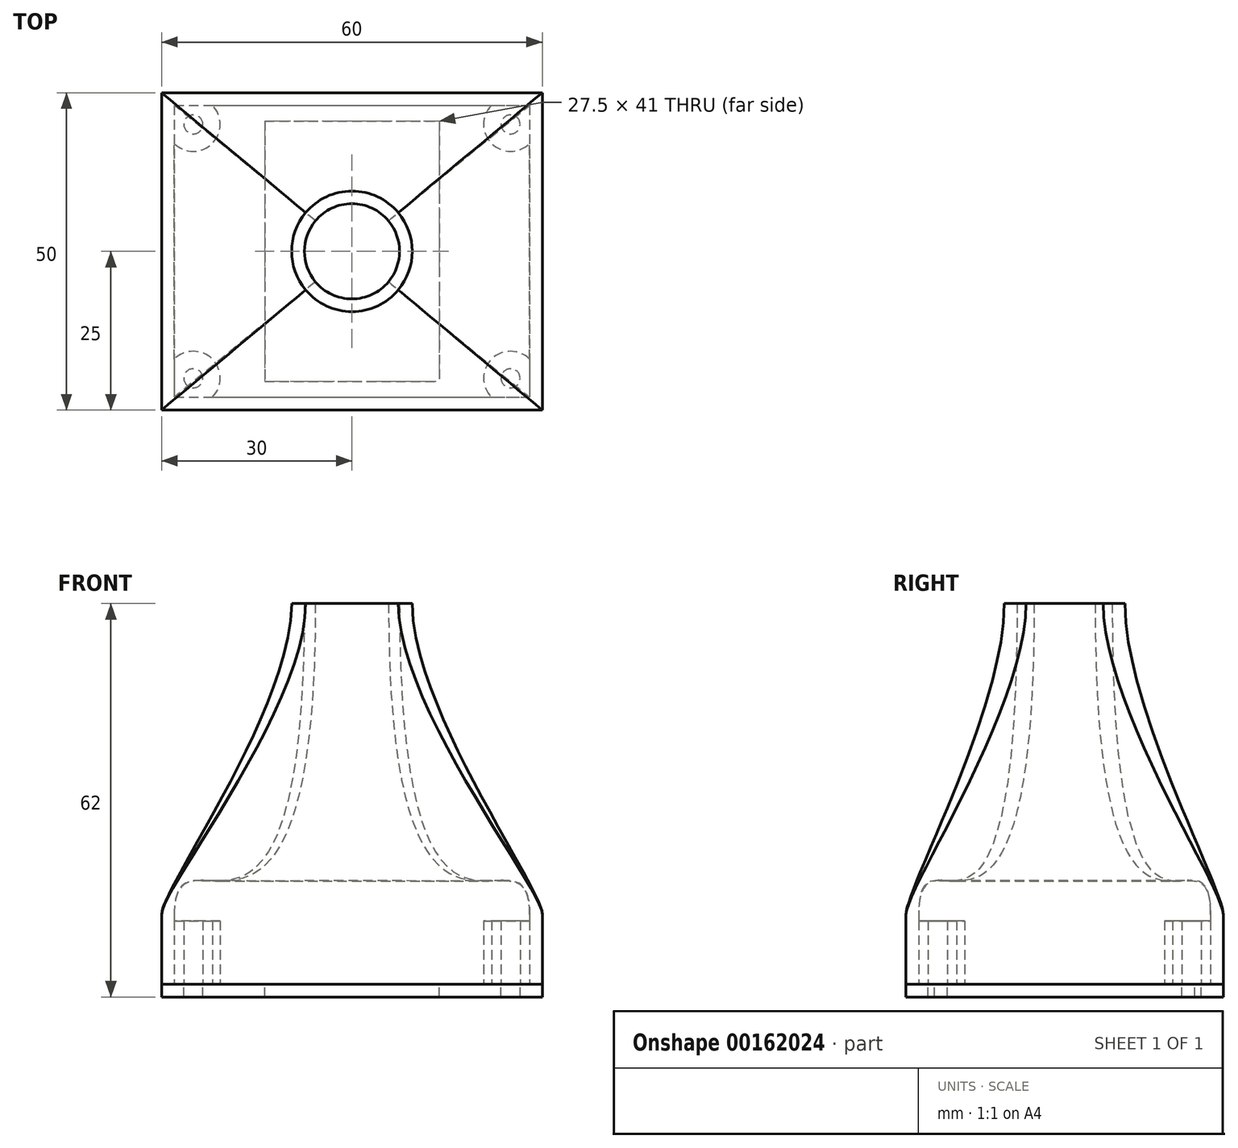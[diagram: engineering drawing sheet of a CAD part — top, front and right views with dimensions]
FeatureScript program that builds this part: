
annotation { "Feature Type Name" : "Feature", "Feature Type Description" : "" }
export const myFeature = defineFeature(function(context is Context, id is Id, definition is map)
    precondition{}
    {
        {
            var Q0;
            Q0=qCreatedBy(makeId("Top.planeOp"),FACE);
            var sketch = newSketch(context, id + "F0", { "sketchPlane" : qUnion([Q0])});
            skLineSegment(sketch, "E0.bottom", {"start": v(0, 0) * mm, "end": v(60, 0) * mm});
            skLineSegment(sketch, "E0.top", {"start": v(0, 50) * mm, "end": v(60, 50) * mm});
            skLineSegment(sketch, "E0.left", {"start": v(0, 0) * mm, "end": v(0, 50) * mm});
            skLineSegment(sketch, "E0.right", {"start": v(60, 0) * mm, "end": v(60, 50) * mm});
            skCircle(sketch, "E1", {"center": v(5, 45) * mm, "radius": 1.5 * mm});
            skCircle(sketch, "E2", {"center": v(55, 45) * mm, "radius": 1.5 * mm});
            skCircle(sketch, "E3", {"center": v(55, 5) * mm, "radius": 1.5 * mm});
            skCircle(sketch, "E4", {"center": v(5, 5) * mm, "radius": 1.5 * mm});
            skLineSegment(sketch, "E5.bottom", {"start": v(16.25, 45.5) * mm, "end": v(43.75, 45.5) * mm});
            skLineSegment(sketch, "E5.top", {"start": v(16.25, 4.5) * mm, "end": v(43.75, 4.5) * mm});
            skLineSegment(sketch, "E5.left", {"start": v(16.25, 45.5) * mm, "end": v(16.25, 4.5) * mm});
            skLineSegment(sketch, "E5.right", {"start": v(43.75, 45.5) * mm, "end": v(43.75, 4.5) * mm});
            skLineSegment(sketch, "E6", {"start": v(30, 50) * mm, "end": v(30, 0) * mm, "construction": true});
            skPoint(sketch, "E6.endSnap0", {"position": v(30, 45.5) * mm});
            skLineSegment(sketch, "E7", {"start": v(0, 25) * mm, "end": v(60, 25) * mm, "construction": true});
            skLineSegment(sketch, "E8", {"start": v(16.25, 45.5) * mm, "end": v(0, 50) * mm, "construction": true});
            skLineSegment(sketch, "E9", {"start": v(16.25, 4.5) * mm, "end": v(0, 0) * mm, "construction": true});
            skLineSegment(sketch, "E10", {"start": v(5, 45) * mm, "end": v(0, 45) * mm, "construction": true});
            skLineSegment(sketch, "E11", {"start": v(5, 5) * mm, "end": v(0, 5) * mm, "construction": true});
            skLineSegment(sketch, "E12", {"start": v(55, 5) * mm, "end": v(60, 5) * mm, "construction": true});
            skLineSegment(sketch, "E13", {"start": v(55, 45) * mm, "end": v(60, 45) * mm, "construction": true});
            skLineSegment(sketch, "E14", {"start": v(5, 45) * mm, "end": v(5, 50) * mm, "construction": true});
            skLineSegment(sketch, "E15", {"start": v(55, 45) * mm, "end": v(55, 50) * mm, "construction": true});
            skLineSegment(sketch, "E16", {"start": v(55, 5) * mm, "end": v(55, 0) * mm, "construction": true});
            skLineSegment(sketch, "E17", {"start": v(5, 5) * mm, "end": v(5, 0) * mm, "construction": true});
            skLineSegment(sketch, "E18.0", {"start": v(2, 48) * mm, "end": v(58, 48) * mm});
            skLineSegment(sketch, "E18.1", {"start": v(2, 2) * mm, "end": v(2, 48) * mm});
            skLineSegment(sketch, "E18.2", {"start": v(2, 2) * mm, "end": v(58, 2) * mm});
            skLineSegment(sketch, "E18.3", {"start": v(58, 2) * mm, "end": v(58, 48) * mm});
            skCircle(sketch, "E19", {"center": v(5, 5) * mm, "radius": 4.24 * mm});
            skCircle(sketch, "E20", {"center": v(55, 5) * mm, "radius": 4.24 * mm});
            skCircle(sketch, "E21", {"center": v(55, 45) * mm, "radius": 4.24 * mm});
            skCircle(sketch, "E22", {"center": v(5, 45) * mm, "radius": 4.24 * mm});
            skSolve(sketch);
        }
        {
            var Q0;
            Q0=makeQuery(id+"F0.imprint","IMPRINT",FACE,{"disambiguationData":[TD([[makeQuery(id+"F0.imprint","IMPRINT",EDGE,{"derivedFrom":sQuery(id+"F0.wireOp",EDGE,"E5.bottom")}),1.0]])]});
            var Q1;
            Q1=makeQuery(id+"F0.imprint","IMPRINT",FACE,{"disambiguationData":[TD([[makeQuery(id+"F0.imprint","IMPRINT",EDGE,{"derivedFrom":sQuery(id+"F0.wireOp",EDGE,"E1")}),-1.0]])]});
            var Q2;
            Q2=makeQuery(id+"F0.imprint","IMPRINT",FACE,{"disambiguationData":[TD([[makeQuery(id+"F0.imprint","IMPRINT",EDGE,{"derivedFrom":sQuery(id+"F0.wireOp",EDGE,"E0.bottom")}),1.0]])]});
            var Q3;
            {var subQ0=sQuery(id+"F0.wireOp",EDGE,"E22");var subQ1=sQuery(id+"F0.wireOp",EDGE,"E18.1");var subQ3=makeQuery(id+"F0.imprint","INTERSECT",VERTEX,{"derivedFrom":[subQ1,subQ0]});Q3=makeQuery(id+"F0.imprint","IMPRINT",FACE,{"disambiguationData":[TD([[makeQuery(id+"F0.imprint","IMPRINT",EDGE,{"disambiguationData":[TD([[subQ3,-1.0]])],"derivedFrom":subQ1}),1.0]])]});}
            var Q4;
            {var subQ0=sQuery(id+"F0.wireOp",EDGE,"E22");var subQ1=sQuery(id+"F0.wireOp",EDGE,"E18.0");var subQ3=makeQuery(id+"F0.imprint","INTERSECT",VERTEX,{"derivedFrom":[subQ1,subQ0]});Q4=makeQuery(id+"F0.imprint","IMPRINT",FACE,{"disambiguationData":[TD([[makeQuery(id+"F0.imprint","IMPRINT",EDGE,{"disambiguationData":[TD([[subQ3,1.0]])],"derivedFrom":subQ1}),1.0]])]});}
            var Q5;
            {var subQ0=sQuery(id+"F0.wireOp",EDGE,"E21");var subQ1=sQuery(id+"F0.wireOp",EDGE,"E18.3");var subQ3=makeQuery(id+"F0.imprint","INTERSECT",VERTEX,{"derivedFrom":[subQ1,subQ0]});Q5=makeQuery(id+"F0.imprint","IMPRINT",FACE,{"disambiguationData":[TD([[makeQuery(id+"F0.imprint","IMPRINT",EDGE,{"disambiguationData":[TD([[subQ3,-1.0]])],"derivedFrom":subQ1}),-1.0]])]});}
            var Q6;
            Q6=makeQuery(id+"F0.imprint","IMPRINT",FACE,{"disambiguationData":[TD([[makeQuery(id+"F0.imprint","IMPRINT",EDGE,{"derivedFrom":sQuery(id+"F0.wireOp",EDGE,"E2")}),-1.0]])]});
            var Q7;
            {var subQ0=sQuery(id+"F0.wireOp",EDGE,"E21");var subQ1=sQuery(id+"F0.wireOp",EDGE,"E18.0");var subQ3=makeQuery(id+"F0.imprint","INTERSECT",VERTEX,{"derivedFrom":[subQ1,subQ0]});Q7=makeQuery(id+"F0.imprint","IMPRINT",FACE,{"disambiguationData":[TD([[makeQuery(id+"F0.imprint","IMPRINT",EDGE,{"disambiguationData":[TD([[subQ3,-1.0]])],"derivedFrom":subQ1}),1.0]])]});}
            var Q8;
            {var subQ0=sQuery(id+"F0.wireOp",EDGE,"E20");var subQ1=sQuery(id+"F0.wireOp",EDGE,"E18.3");var subQ3=makeQuery(id+"F0.imprint","INTERSECT",VERTEX,{"derivedFrom":[subQ1,subQ0]});Q8=makeQuery(id+"F0.imprint","IMPRINT",FACE,{"disambiguationData":[TD([[makeQuery(id+"F0.imprint","IMPRINT",EDGE,{"disambiguationData":[TD([[subQ3,1.0]])],"derivedFrom":subQ1}),-1.0]])]});}
            var Q9;
            Q9=makeQuery(id+"F0.imprint","IMPRINT",FACE,{"disambiguationData":[TD([[makeQuery(id+"F0.imprint","IMPRINT",EDGE,{"derivedFrom":sQuery(id+"F0.wireOp",EDGE,"E3")}),-1.0]])]});
            var Q10;
            {var subQ0=sQuery(id+"F0.wireOp",EDGE,"E20");var subQ1=sQuery(id+"F0.wireOp",EDGE,"E18.2");var subQ3=makeQuery(id+"F0.imprint","INTERSECT",VERTEX,{"derivedFrom":[subQ1,subQ0]});Q10=makeQuery(id+"F0.imprint","IMPRINT",FACE,{"disambiguationData":[TD([[makeQuery(id+"F0.imprint","IMPRINT",EDGE,{"disambiguationData":[TD([[subQ3,-1.0]])],"derivedFrom":subQ1}),-1.0]])]});}
            var Q11;
            Q11=makeQuery(id+"F0.imprint","IMPRINT",FACE,{"disambiguationData":[TD([[makeQuery(id+"F0.imprint","IMPRINT",EDGE,{"derivedFrom":sQuery(id+"F0.wireOp",EDGE,"E4")}),-1.0]])]});
            var Q12;
            {var subQ0=sQuery(id+"F0.wireOp",EDGE,"E19");var subQ1=sQuery(id+"F0.wireOp",EDGE,"E18.1");var subQ3=makeQuery(id+"F0.imprint","INTERSECT",VERTEX,{"derivedFrom":[subQ1,subQ0]});Q12=makeQuery(id+"F0.imprint","IMPRINT",FACE,{"disambiguationData":[TD([[makeQuery(id+"F0.imprint","IMPRINT",EDGE,{"disambiguationData":[TD([[subQ3,1.0]])],"derivedFrom":subQ1}),1.0]])]});}
            var Q13;
            {var subQ0=sQuery(id+"F0.wireOp",EDGE,"E19");var subQ1=sQuery(id+"F0.wireOp",EDGE,"E18.2");var subQ3=makeQuery(id+"F0.imprint","INTERSECT",VERTEX,{"derivedFrom":[subQ1,subQ0]});Q13=makeQuery(id+"F0.imprint","IMPRINT",FACE,{"disambiguationData":[TD([[makeQuery(id+"F0.imprint","IMPRINT",EDGE,{"disambiguationData":[TD([[subQ3,1.0]])],"derivedFrom":subQ1}),-1.0]])]});}
            extrude(context, id + "F1", {"entities" : qUnion([Q0, Q1, Q2, Q3, Q4, Q5, Q6, Q7, Q8, Q9, Q10, Q11, Q12, Q13]), "oppositeDirection" : true, "depth" : 2 * mm});
        }
        {
            var Q0;
            Q0=makeQuery(id+"F0.imprint","IMPRINT",FACE,{"disambiguationData":[TD([[makeQuery(id+"F0.imprint","IMPRINT",EDGE,{"derivedFrom":sQuery(id+"F0.wireOp",EDGE,"E0.bottom")}),1.0]])]});
            var Q1;
            {var subQ0=sQuery(id+"F0.wireOp",EDGE,"E21");var subQ1=sQuery(id+"F0.wireOp",EDGE,"E18.3");var subQ3=makeQuery(id+"F0.imprint","INTERSECT",VERTEX,{"derivedFrom":[subQ1,subQ0]});Q1=makeQuery(id+"F0.imprint","IMPRINT",FACE,{"disambiguationData":[TD([[makeQuery(id+"F0.imprint","IMPRINT",EDGE,{"disambiguationData":[TD([[subQ3,-1.0]])],"derivedFrom":subQ1}),-1.0]])]});}
            var Q2;
            Q2=makeQuery(id+"F0.imprint","IMPRINT",FACE,{"disambiguationData":[TD([[makeQuery(id+"F0.imprint","IMPRINT",EDGE,{"derivedFrom":sQuery(id+"F0.wireOp",EDGE,"E2")}),-1.0]])]});
            var Q3;
            {var subQ0=sQuery(id+"F0.wireOp",EDGE,"E21");var subQ1=sQuery(id+"F0.wireOp",EDGE,"E18.0");var subQ3=makeQuery(id+"F0.imprint","INTERSECT",VERTEX,{"derivedFrom":[subQ1,subQ0]});Q3=makeQuery(id+"F0.imprint","IMPRINT",FACE,{"disambiguationData":[TD([[makeQuery(id+"F0.imprint","IMPRINT",EDGE,{"disambiguationData":[TD([[subQ3,-1.0]])],"derivedFrom":subQ1}),1.0]])]});}
            var Q4;
            {var subQ0=sQuery(id+"F0.wireOp",EDGE,"E20");var subQ1=sQuery(id+"F0.wireOp",EDGE,"E18.2");var subQ3=makeQuery(id+"F0.imprint","INTERSECT",VERTEX,{"derivedFrom":[subQ1,subQ0]});Q4=makeQuery(id+"F0.imprint","IMPRINT",FACE,{"disambiguationData":[TD([[makeQuery(id+"F0.imprint","IMPRINT",EDGE,{"disambiguationData":[TD([[subQ3,-1.0]])],"derivedFrom":subQ1}),-1.0]])]});}
            var Q5;
            {var subQ0=sQuery(id+"F0.wireOp",EDGE,"E20");var subQ1=sQuery(id+"F0.wireOp",EDGE,"E18.3");var subQ3=makeQuery(id+"F0.imprint","INTERSECT",VERTEX,{"derivedFrom":[subQ1,subQ0]});Q5=makeQuery(id+"F0.imprint","IMPRINT",FACE,{"disambiguationData":[TD([[makeQuery(id+"F0.imprint","IMPRINT",EDGE,{"disambiguationData":[TD([[subQ3,1.0]])],"derivedFrom":subQ1}),-1.0]])]});}
            var Q6;
            Q6=makeQuery(id+"F0.imprint","IMPRINT",FACE,{"disambiguationData":[TD([[makeQuery(id+"F0.imprint","IMPRINT",EDGE,{"derivedFrom":sQuery(id+"F0.wireOp",EDGE,"E3")}),-1.0]])]});
            var Q7;
            {var subQ0=sQuery(id+"F0.wireOp",EDGE,"E19");var subQ1=sQuery(id+"F0.wireOp",EDGE,"E18.1");var subQ3=makeQuery(id+"F0.imprint","INTERSECT",VERTEX,{"derivedFrom":[subQ1,subQ0]});Q7=makeQuery(id+"F0.imprint","IMPRINT",FACE,{"disambiguationData":[TD([[makeQuery(id+"F0.imprint","IMPRINT",EDGE,{"disambiguationData":[TD([[subQ3,1.0]])],"derivedFrom":subQ1}),1.0]])]});}
            var Q8;
            Q8=makeQuery(id+"F0.imprint","IMPRINT",FACE,{"disambiguationData":[TD([[makeQuery(id+"F0.imprint","IMPRINT",EDGE,{"derivedFrom":sQuery(id+"F0.wireOp",EDGE,"E4")}),-1.0]])]});
            var Q9;
            {var subQ0=sQuery(id+"F0.wireOp",EDGE,"E19");var subQ1=sQuery(id+"F0.wireOp",EDGE,"E18.2");var subQ3=makeQuery(id+"F0.imprint","INTERSECT",VERTEX,{"derivedFrom":[subQ1,subQ0]});Q9=makeQuery(id+"F0.imprint","IMPRINT",FACE,{"disambiguationData":[TD([[makeQuery(id+"F0.imprint","IMPRINT",EDGE,{"disambiguationData":[TD([[subQ3,1.0]])],"derivedFrom":subQ1}),-1.0]])]});}
            var Q10;
            {var subQ0=sQuery(id+"F0.wireOp",EDGE,"E22");var subQ1=sQuery(id+"F0.wireOp",EDGE,"E18.0");var subQ3=makeQuery(id+"F0.imprint","INTERSECT",VERTEX,{"derivedFrom":[subQ1,subQ0]});Q10=makeQuery(id+"F0.imprint","IMPRINT",FACE,{"disambiguationData":[TD([[makeQuery(id+"F0.imprint","IMPRINT",EDGE,{"disambiguationData":[TD([[subQ3,1.0]])],"derivedFrom":subQ1}),1.0]])]});}
            var Q11;
            Q11=makeQuery(id+"F0.imprint","IMPRINT",FACE,{"disambiguationData":[TD([[makeQuery(id+"F0.imprint","IMPRINT",EDGE,{"derivedFrom":sQuery(id+"F0.wireOp",EDGE,"E1")}),-1.0]])]});
            var Q12;
            {var subQ0=sQuery(id+"F0.wireOp",EDGE,"E22");var subQ1=sQuery(id+"F0.wireOp",EDGE,"E18.1");var subQ3=makeQuery(id+"F0.imprint","INTERSECT",VERTEX,{"derivedFrom":[subQ1,subQ0]});Q12=makeQuery(id+"F0.imprint","IMPRINT",FACE,{"disambiguationData":[TD([[makeQuery(id+"F0.imprint","IMPRINT",EDGE,{"disambiguationData":[TD([[subQ3,-1.0]])],"derivedFrom":subQ1}),1.0]])]});}
            extrude(context, id + "F2", {"entities" : qUnion([Q0, Q1, Q2, Q3, Q4, Q5, Q6, Q7, Q8, Q9, Q10, Q11, Q12]), "depth" : 10 * mm});
        }
        {
            var Q0;
            Q0=makeQuery(id+"F2.opExtrude","CAP_FACE",FACE,{"disambiguationData":[OSD([sQuery(id+"F0.wireOp",EDGE,"E0.bottom"),sQuery(id+"F0.wireOp",EDGE,"E0.top"),sQuery(id+"F0.wireOp",EDGE,"E0.left"),sQuery(id+"F0.wireOp",EDGE,"E0.right"),sQuery(id+"F0.wireOp",EDGE,"E1"),sQuery(id+"F0.wireOp",EDGE,"E2"),sQuery(id+"F0.wireOp",EDGE,"E3"),sQuery(id+"F0.wireOp",EDGE,"E4"),sQuery(id+"F0.wireOp",EDGE,"E18.0"),sQuery(id+"F0.wireOp",EDGE,"E18.1"),sQuery(id+"F0.wireOp",EDGE,"E18.2"),sQuery(id+"F0.wireOp",EDGE,"E18.3"),sQuery(id+"F0.wireOp",EDGE,"E19"),sQuery(id+"F0.wireOp",EDGE,"E20"),sQuery(id+"F0.wireOp",EDGE,"E21"),sQuery(id+"F0.wireOp",EDGE,"E22")])],"isStart":false});
            cPlane(context, id + "F3", {"entities" : qUnion([Q0]), "cplaneType" : CPlaneType.OFFSET, "offset" : 50 * mm, "width" : 150 * mm, "height" : 150 * mm});
        }
        {
            var Q0;
            Q0=qCreatedBy(id+"F3.planeOp",FACE);
            var sketch = newSketch(context, id + "F4", { "sketchPlane" : qUnion([Q0])});
            skLineSegment(sketch, "E23.bottom", {"start": v(0, 0) * mm, "end": v(60, 0) * mm, "construction": true});
            skLineSegment(sketch, "E23.top", {"start": v(0, 50) * mm, "end": v(60, 50) * mm});
            skLineSegment(sketch, "E23.left", {"start": v(0, 0) * mm, "end": v(0, 50) * mm, "construction": true});
            skLineSegment(sketch, "E23.right", {"start": v(60, 0) * mm, "end": v(60, 50) * mm, "construction": true});
            skLineSegment(sketch, "E24", {"start": v(0, 50) * mm, "end": v(60, 0) * mm, "construction": true});
            skCircle(sketch, "E25", {"center": v(30, 25) * mm, "radius": 7.5 * mm, "construction": true});
            skLineSegment(sketch, "E26", {"start": v(0, 0) * mm, "end": v(60, 50) * mm, "construction": true});
            skArc(sketch, "E27", {"start": v(22.7, 31.08) * mm, "mid": v(20.5, 25) * mm, "end": v(22.7, 18.92) * mm});
            skArc(sketch, "E28", {"start": v(37.3, 31.08) * mm, "mid": v(30, 34.5) * mm, "end": v(22.7, 31.08) * mm});
            skArc(sketch, "E29", {"start": v(37.3, 18.92) * mm, "mid": v(39.5, 25) * mm, "end": v(37.3, 31.08) * mm});
            skArc(sketch, "E30", {"start": v(22.7, 18.92) * mm, "mid": v(30, 15.5) * mm, "end": v(37.3, 18.92) * mm});
            skSolve(sketch);
        }
        {
            var Q0;
            Q0=makeQuery(id+"F2.opExtrude","CAP_FACE",FACE,{"disambiguationData":[OSD([sQuery(id+"F0.wireOp",EDGE,"E0.bottom"),sQuery(id+"F0.wireOp",EDGE,"E0.top"),sQuery(id+"F0.wireOp",EDGE,"E0.left"),sQuery(id+"F0.wireOp",EDGE,"E0.right"),sQuery(id+"F0.wireOp",EDGE,"E1"),sQuery(id+"F0.wireOp",EDGE,"E2"),sQuery(id+"F0.wireOp",EDGE,"E3"),sQuery(id+"F0.wireOp",EDGE,"E4"),sQuery(id+"F0.wireOp",EDGE,"E18.0"),sQuery(id+"F0.wireOp",EDGE,"E18.1"),sQuery(id+"F0.wireOp",EDGE,"E18.2"),sQuery(id+"F0.wireOp",EDGE,"E18.3"),sQuery(id+"F0.wireOp",EDGE,"E19"),sQuery(id+"F0.wireOp",EDGE,"E20"),sQuery(id+"F0.wireOp",EDGE,"E21"),sQuery(id+"F0.wireOp",EDGE,"E22")])],"isStart":false});
            var sketch = newSketch(context, id + "F5", { "sketchPlane" : qUnion([Q0])});
            skLineSegment(sketch, "E31.bottom", {"start": v(0, 50) * mm, "end": v(60, 50) * mm});
            skLineSegment(sketch, "E31.top", {"start": v(0, 0) * mm, "end": v(60, 0) * mm});
            skLineSegment(sketch, "E31.left", {"start": v(0, 50) * mm, "end": v(0, 0) * mm});
            skLineSegment(sketch, "E31.right", {"start": v(60, 50) * mm, "end": v(60, 0) * mm});
            skLineSegment(sketch, "E32.0", {"start": v(2, 48) * mm, "end": v(58, 48) * mm});
            skLineSegment(sketch, "E32.1", {"start": v(2, 48) * mm, "end": v(2, 2) * mm});
            skLineSegment(sketch, "E32.2", {"start": v(2, 2) * mm, "end": v(58, 2) * mm});
            skLineSegment(sketch, "E32.3", {"start": v(58, 48) * mm, "end": v(58, 2) * mm});
            skSolve(sketch);
        }
        {
            var Q0;
            Q0 = qSketchRegion(id + "F5", true);
            extrude(context, id + "F6", {"entities" : qUnion([Q0]), "operationType" : NewBodyOperationType.ADD, "depth" : 1 * mm});
        }
        {
            var Q0;
            Q0=makeQuery(id+"F6.opExtrude","CAP_FACE",FACE,{"disambiguationData":[OSD([sQuery(id+"F5.wireOp",EDGE,"E31.bottom"),sQuery(id+"F5.wireOp",EDGE,"E31.top"),sQuery(id+"F5.wireOp",EDGE,"E31.left"),sQuery(id+"F5.wireOp",EDGE,"E31.right"),sQuery(id+"F5.wireOp",EDGE,"E32.0"),sQuery(id+"F5.wireOp",EDGE,"E32.1"),sQuery(id+"F5.wireOp",EDGE,"E32.2"),sQuery(id+"F5.wireOp",EDGE,"E32.3")])],"isStart":false});
            var sketch = newSketch(context, id + "F7", { "sketchPlane" : qUnion([Q0])});
            skLineSegment(sketch, "E33.0", {"start": v(0, 0) * mm, "end": v(0, 50) * mm});
            skLineSegment(sketch, "E33.1", {"start": v(0, 0) * mm, "end": v(60, 0) * mm});
            skLineSegment(sketch, "E33.2", {"start": v(60, 0) * mm, "end": v(60, 50) * mm});
            skLineSegment(sketch, "E33.3", {"start": v(0, 50) * mm, "end": v(60, 50) * mm});
            skSolve(sketch);
        }
        {
            var Q1;
            Q1 = qSketchRegion(id + "F7", true);
            var Q2;
            Q2 = qSketchRegion(id + "F4", true);
            loft(context, id + "F8", {"operationType" : NewBodyOperationType.ADD, "startCondition" : LoftEndDerivativeType.NORMAL_TO_PROFILE, "startMagnitude" : .25, "endCondition" : LoftEndDerivativeType.NORMAL_TO_PROFILE, "endMagnitude" : 1, "sheetProfilesArray" : [{ "sheetProfileEntities" : qUnion([Q1]) }, { "sheetProfileEntities" : qUnion([Q2]) }]});
        }
        {
            var Q0;
            Q0=makeQuery(id+"F8.opLoft","CAP_FACE",FACE,{"disambiguationData":[OSD([makeQuery(id+"F4.imprint","IMPRINT",FACE,{"disambiguationData":[TD([[makeQuery(id+"F4.imprint","IMPRINT",EDGE,{"derivedFrom":sQuery(id+"F4.wireOp",EDGE,"E27")}),1.0]])]})])],"isStart":true});
            var sketch = newSketch(context, id + "F9", { "sketchPlane" : qUnion([Q0])});
            skArc(sketch, "E34", {"start": v(35.76, 29.8) * mm, "mid": v(30, 32.5) * mm, "end": v(24.24, 29.8) * mm});
            skArc(sketch, "E35", {"start": v(24.24, 20.2) * mm, "mid": v(30, 17.5) * mm, "end": v(35.76, 20.2) * mm});
            skArc(sketch, "E36", {"start": v(24.24, 29.8) * mm, "mid": v(22.5, 25) * mm, "end": v(24.24, 20.2) * mm});
            skArc(sketch, "E37", {"start": v(35.76, 20.2) * mm, "mid": v(37.5, 25) * mm, "end": v(35.76, 29.8) * mm});
            skSolve(sketch);
        }
        {
            var Q1;
            Q1=makeQuery(id+"F9.imprint","IMPRINT",FACE,{"disambiguationData":[TD([[makeQuery(id+"F9.imprint","IMPRINT",EDGE,{"derivedFrom":sQuery(id+"F9.wireOp",EDGE,"E34")}),1.0]])]});
            var Q2;
            Q2=makeQuery(id+"F8.opLoft","CAP_FACE",FACE,{"disambiguationData":[OSD([makeQuery(id+"F7.imprint","IMPRINT",FACE,{"disambiguationData":[TD([[makeQuery(id+"F7.imprint","IMPRINT",EDGE,{"derivedFrom":makeQuery(id+"F6.opExtrude","CAP_EDGE",EDGE,{"disambiguationData":[OSD([sQuery(id+"F5.wireOp",EDGE,"E32.0")])],"isStart":false})}),-1.0]])]})])],"isStart":true});
            loft(context, id + "F10", {"operationType" : NewBodyOperationType.REMOVE, "startCondition" : LoftEndDerivativeType.NORMAL_TO_PROFILE, "startMagnitude" : 4, "endCondition" : LoftEndDerivativeType.NORMAL_TO_PROFILE, "endMagnitude" : 1, "sheetProfilesArray" : [{ "sheetProfileEntities" : qUnion([Q1]) }, { "sheetProfileEntities" : qUnion([Q2]) }]});
        }
    });
